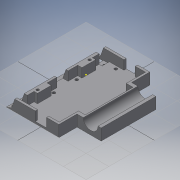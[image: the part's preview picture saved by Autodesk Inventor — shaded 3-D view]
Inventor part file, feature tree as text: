
AUTODESK INVENTOR PART (.ipt)
format: ipt  version: 2016 (Build 200138000, 138)  size: 394,752 bytes
history: native  units: in
note: dims shown in document units (in); Inventor stores cm internally (conversion verified against a paired STEP export)
features: sketch x18, extrude x17
ambient origin geometry x8: Origin, YZ Plane, XZ Plane, XY Plane, X Axis, Y Axis, Z Axis, Center Point
bodies: Solid1 (feature_tree)
feature tree (35):
  extrude  "Extrusion1"  Depth=4.0in
  extrude  "Extrusion2"  Depth=1.2in
  extrude  "Extrusion3"  Depth=0.8in
  sketch  "Sketch4"  dims[d7=1.8125in d8=0.0in d9=0.65in]
  extrude  "Extrusion4"  Depth=0.65in
  extrude  "Extrusion5"  Depth=0.5in TaperAngle=0.0deg
  extrude  "Extrusion6"  Depth=0.25in
  extrude  "Extrusion7"  Depth=1.0in
  extrude  "Extrusion8"  Depth=4.9375in TaperAngle=0.0deg
  extrude  "Extrusion9"  Depth=1.35in
  extrude  "Extrusion10"  Depth=0.1in
  extrude  "Extrusion11"  Depth=0.85in
  extrude  "Extrusion12"  Depth=0.85in
  extrude  "Extrusion13"  Depth=1.325in
  extrude  "Extrusion14"  Depth=0.15in
  extrude  "Extrusion15"  Depth=0.4in TaperAngle=0.0deg
  extrude  "Extrusion16"  Depth=0.13in
  extrude  "Extrusion17"  Depth=0.175in
  sketch  "Sketch1"  dims[d0=4.0in d1=4.0in]
  sketch  "Sketch2"  dims[d2=1.0in d3=0.0in d4=1.2in]
  sketch  "Sketch3"  dims[d5=0.8in d6=0.8in]
  sketch  "Sketch5"  dims[d10=0.5in d11=2.9375in d12=0.0in]
  sketch  "Sketch6"  dims[d13=0.5in d14=0.25in]
  sketch  "Sketch7"  dims[d15=1.0857in d16=1.0in]
  sketch  "Sketch8"  dims[d17=0.8933in d18=4.9375in d19=0.0in]
  sketch  "Sketch9"  dims[d20=7.75in d21=0.0in d22=1.35in]
  sketch  "Sketch10"  dims[d23=0.85in d24=0.1in]
  sketch  "Sketch11"  dims[d25=0.5in d26=0.85in]
  sketch  "Sketch12"  dims[d27=0.1in d28=0.85in]
  sketch  "Sketch13"  dims[d29=1.35in d30=1.325in]
  sketch  "Sketch14"  dims[d31=0.15in d32=1.2681in]
  sketch  "Sketch15"  dims[d33=2.1in d34=0.4in d35=0.0in]
  sketch  "Sketch16"  dims[d36=0.13in d37=0.13in]
  sketch  "Sketch17"  dims[d38=1.0in d39=0.175in]
  sketch  "Sketch18"  dims[d40=0.13in d41=0.13in d42=0.13in d43=0.13in d44=0.175in d45=0.13in d46=0.175in d47=0.13in d48=0.13in d49=0.13in d50=0.85in d51=0.0in d52=0.9625in d53=0.0in d54=2.525in d55=0.0in d56=0.52in d57=0.32in d59=0.42in d60=0.1in d61=0.32in d62=0.1in d63=0.475in d64=0.0in d65=0.09in d66=0.065in d67=0.09in d68=1.025in d69=0.0in d70=0.02in d71=0.265in d72=0.1512in d73=4.0in d74=0.0in d75=1.8125in d76=0.0in d77=0.118in d78=0.118in d79=2.2835in d80=0.15in d81=0.15in d82=0.8585in d83=0.25in d84=0.0in d85=0.3in d86=0.15in d87=0.3in d88=0.3in d89=0.15in d90=0.4in d91=0.0in d92=0.4in d93=0.0in d94=0.5in d95=1.75in d96=0.5in d97=0.45in d98=0.4in d99=0.0in]
